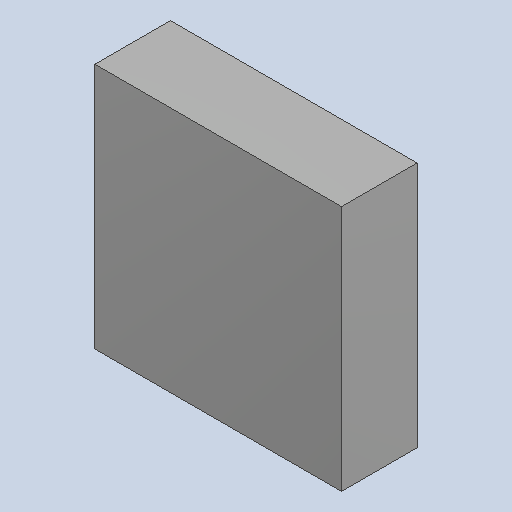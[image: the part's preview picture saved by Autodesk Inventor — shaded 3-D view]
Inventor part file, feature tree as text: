
AUTODESK INVENTOR PART (.ipt)
format: ipt  version: 2023.4 (Build 274418000, 418)  size: 82,432 bytes
history: native  units: mm
features: extrude x1
ambient origin geometry x8: Origin, YZ Plane, XZ Plane, XY Plane, X Axis, Y Axis, Z Axis, Center Point
bodies: Solid1 (feature_tree)
feature tree (1):
  extrude  "Extruded"  [1 undecoded]
note: 1 required parameter value undecoded (feature->parameter linkage not recoverable at this tier; creation-order binding heuristic only, values carry confidence <= 0.55)
